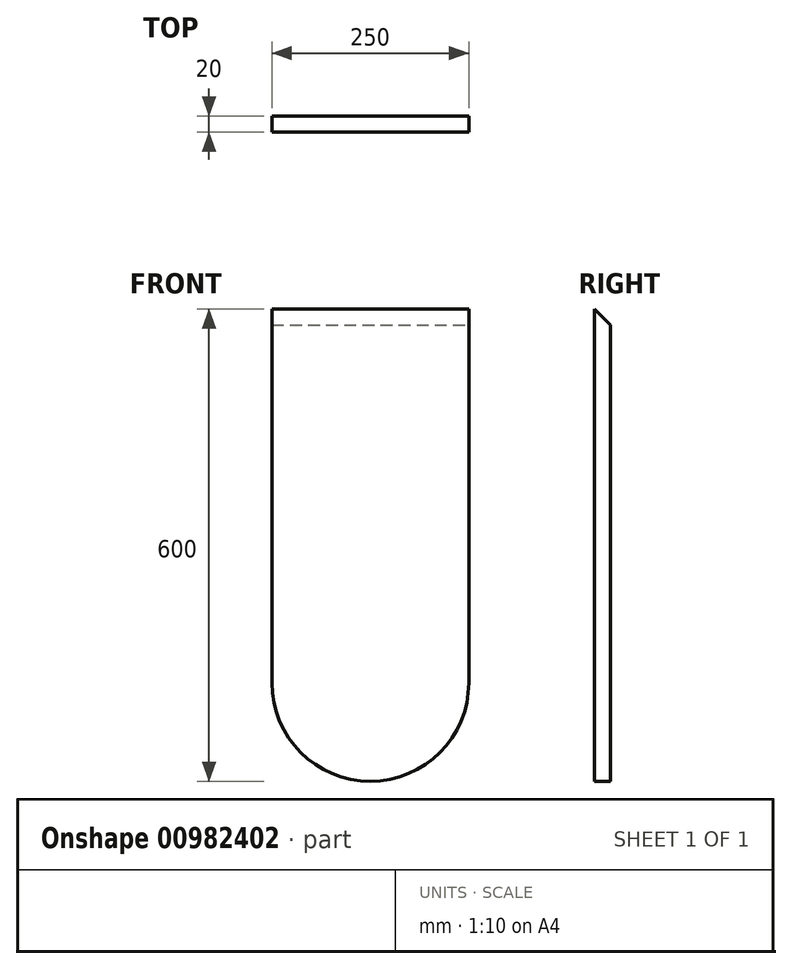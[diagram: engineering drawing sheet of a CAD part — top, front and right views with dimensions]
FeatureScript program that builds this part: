
annotation { "Feature Type Name" : "Feature", "Feature Type Description" : "" }
export const myFeature = defineFeature(function(context is Context, id is Id, definition is map)
    precondition{}
    {
        {
            var Q0;
            Q0=qCreatedBy(makeId("Front.planeOp"),FACE);
            var sketch = newSketch(context, id + "F0", { "sketchPlane" : qUnion([Q0])});
            skArc(sketch, "E0", {"start": v(-126.21, 0) * mm, "mid": v(-1.21, -125) * mm, "end": v(123.79, 0) * mm});
            skLineSegment(sketch, "E1", {"start": v(-126.21, 0) * mm, "end": v(-126.21, 475) * mm});
            skLineSegment(sketch, "E2", {"start": v(-126.21, 475) * mm, "end": v(123.79, 475) * mm});
            skLineSegment(sketch, "E3", {"start": v(123.79, 475) * mm, "end": v(123.79, 0) * mm});
            skLineSegment(sketch, "E4", {"start": v(-126.21, 0) * mm, "end": v(123.79, 0) * mm});
            skLineSegment(sketch, "E5", {"start": v(-1.21, -125) * mm, "end": v(205.67, -125) * mm, "construction": true});
            skSolve(sketch);
        }
        {
            var Q0;
            Q0=makeQuery(id+"F0.imprint","IMPRINT",FACE,{"disambiguationData":[TD([[makeQuery(id+"F0.imprint","IMPRINT",EDGE,{"derivedFrom":sQuery(id+"F0.wireOp",EDGE,"E0")}),1.0]])]});
            extrude(context, id + "F1", {"entities" : qUnion([Q0]), "depth" : 20 * mm, "offsetDistance" : 25 * mm});
        }
        {
            var Q0;
            Q0=makeQuery(id+"F0.imprint","IMPRINT",FACE,{"disambiguationData":[TD([[makeQuery(id+"F0.imprint","IMPRINT",EDGE,{"derivedFrom":sQuery(id+"F0.wireOp",EDGE,"E1")}),-1.0]])]});
            extrude(context, id + "F2", {"entities" : qUnion([Q0]), "operationType" : NewBodyOperationType.ADD, "depth" : 20 * mm, "offsetDistance" : 25 * mm});
        }
        {
            var Q0;
            Q0=makeQuery(id+"F2.opExtrude","CAP_EDGE",EDGE,{"disambiguationData":[OSD([sQuery(id+"F0.wireOp",EDGE,"E2")])],"isStart":true});
            chamfer(context, id + "F3", {"entities" : qUnion([Q0]), "width" : 20 * mm, "tangentPropagation" : true});
        }
    });
